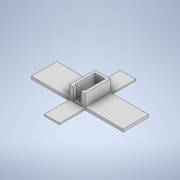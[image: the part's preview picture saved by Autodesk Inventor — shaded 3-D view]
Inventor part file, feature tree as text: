
AUTODESK INVENTOR PART (.ipt)
format: ipt  version: 2021.2 (Build 252289000, 289)  size: 172,032 bytes
history: native  units: in
note: dims shown in document units (in); Inventor stores cm internally (conversion verified against a paired STEP export)
features: extrude x8, sketch x8
ambient origin geometry x8: Origin, YZ Plane, XZ Plane, XY Plane, X Axis, Y Axis, Z Axis, Center Point
bodies: Solid1 (feature_tree)
feature tree (16):
  extrude  "Extrusion1"  Depth=1.5906in
  extrude  "Extrusion2"  Depth=0.2in
  extrude  "Extrusion3"  Depth=0.2in
  extrude  "Extrusion4"  Depth=0.6in
  extrude  "Extrusion5"  Depth=0.14in TaperAngle=0.0deg
  extrude  "Extrusion6"  Depth=3.0in TaperAngle=0.0deg
  extrude  "Extrusion7"  Depth=2.0in TaperAngle=0.0deg
  extrude  "Extrusion8"  Depth=2.0in TaperAngle=0.0deg
  sketch  "Sketch1"  dims[d0=0.8071in d1=1.5906in]
  sketch  "Sketch2"  dims[d2=0.2in d3=0.2in]
  sketch  "Sketch3"  dims[d4=0.2in d5=0.2in]
  sketch  "Sketch4"  dims[d6=0.9843in d7=0.0in d8=0.6in]
  sketch  "Sketch5"  dims[d9=0.9843in d10=0.0in d11=0.14in d12=0.0in]
  sketch  "Sketch6"  dims[d13=3.0in d14=0.0in d15=3.0in d16=0.0in]
  sketch  "Sketch7"  dims[d17=0.1in d18=2.0in d19=0.0in]
  sketch  "Sketch8"  dims[d20=2.0in d21=0.0in d22=1.0in d23=0.0in]
